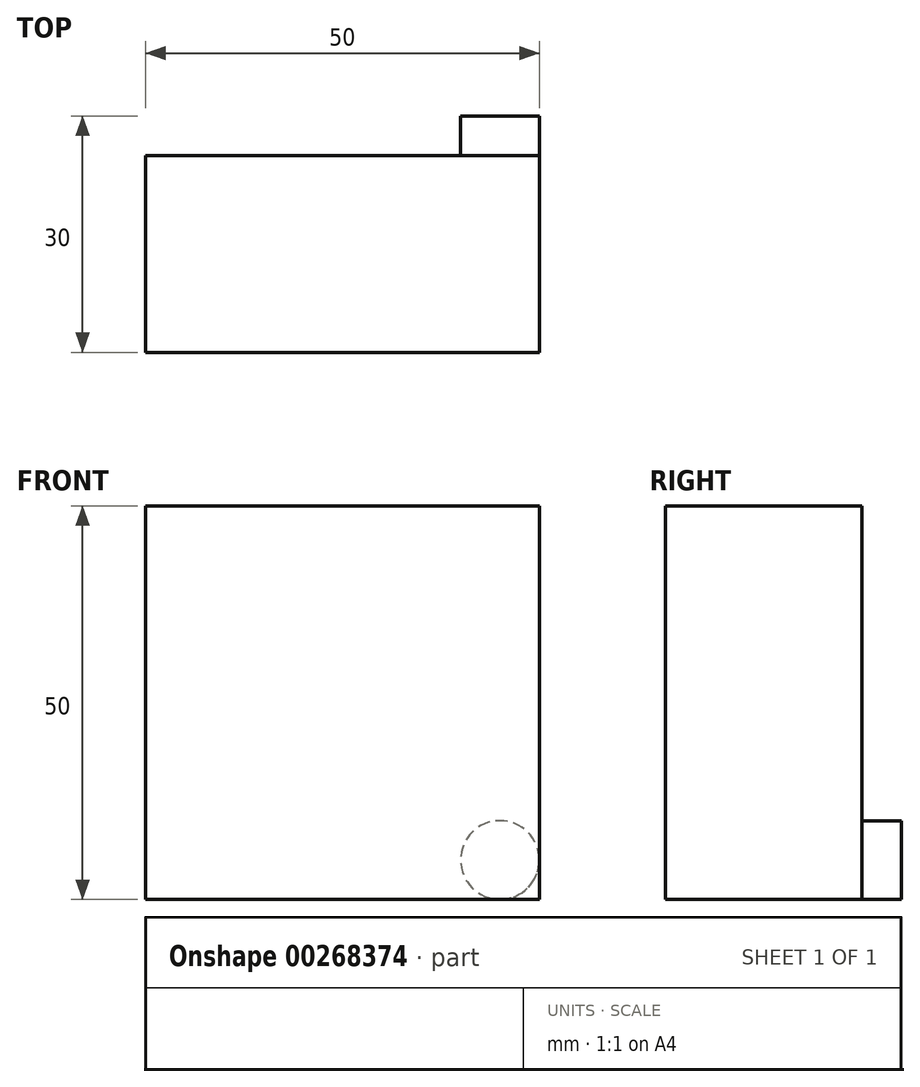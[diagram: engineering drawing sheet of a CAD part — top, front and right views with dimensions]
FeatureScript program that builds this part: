
annotation { "Feature Type Name" : "Feature", "Feature Type Description" : "" }
export const myFeature = defineFeature(function(context is Context, id is Id, definition is map)
    precondition{}
    {
        {
            var Q0;
            Q0=qCreatedBy(makeId("Front.planeOp"),FACE);
            var sketch = newSketch(context, id + "F0", { "sketchPlane" : qUnion([Q0])});
            skLineSegment(sketch, "E0.bottom", {"start": v(25, 25) * mm, "end": v(-25, 25) * mm});
            skLineSegment(sketch, "E0.top", {"start": v(25, -25) * mm, "end": v(-25, -25) * mm});
            skLineSegment(sketch, "E0.left", {"start": v(25, 25) * mm, "end": v(25, -25) * mm});
            skLineSegment(sketch, "E0.right", {"start": v(-25, 25) * mm, "end": v(-25, -25) * mm});
            skPoint(sketch, "E0.middle", {"position": v(0, 0) * mm});
            skCircle(sketch, "E1", {"center": v(20, -20) * mm, "radius": 5 * mm});
            skSolve(sketch);
        }
        {
            var Q0;
            {var subQ2=sQuery(id+"F0.wireOp",EDGE,"E0.bottom");Q0=makeQuery(id+"F0.imprint","IMPRINT",FACE,{"disambiguationData":[TD([[makeQuery(id+"F0.imprint","IMPRINT",EDGE,{"derivedFrom":subQ2}),1.0]])]});}
            var Q1;
            {var subQ0=sQuery(id+"F0.wireOp",EDGE,"E0.left");var subQ1=sQuery(id+"F0.wireOp",EDGE,"E0.top");var subQ2=makeQuery(id+"F0.imprint","INTERSECT",VERTEX,{"derivedFrom":[subQ1,subQ0]});Q1=makeQuery(id+"F0.imprint","IMPRINT",FACE,{"disambiguationData":[TD([[makeQuery(id+"F0.imprint","IMPRINT",EDGE,{"disambiguationData":[TD([[subQ2,-1.0]])],"derivedFrom":subQ1}),-1.0]])]});}
            var Q2;
            {var subQ0=sQuery(id+"F0.wireOp",EDGE,"E1");var subQ1=makeQuery(id+"F0.imprint","INTERSECT",VERTEX,{"derivedFrom":[sQuery(id+"F0.wireOp",EDGE,"E0.top"),subQ0]});Q2=makeQuery(id+"F0.imprint","IMPRINT",FACE,{"disambiguationData":[TD([[makeQuery(id+"F0.imprint","IMPRINT",EDGE,{"disambiguationData":[TD([[subQ1,1.0]])],"derivedFrom":subQ0}),1.0]])]});}
            extrude(context, id + "F1", {"entities" : qUnion([Q0, Q1, Q2]), "depth" : 25 * mm});
        }
        {
            var Q0;
            {var subQ0=sQuery(id+"F0.wireOp",EDGE,"E1");var subQ1=makeQuery(id+"F0.imprint","INTERSECT",VERTEX,{"derivedFrom":[sQuery(id+"F0.wireOp",EDGE,"E0.top"),subQ0]});Q0=makeQuery(id+"F0.imprint","IMPRINT",FACE,{"disambiguationData":[TD([[makeQuery(id+"F0.imprint","IMPRINT",EDGE,{"disambiguationData":[TD([[subQ1,1.0]])],"derivedFrom":subQ0}),1.0]])]});}
            var Q1;
            Q1=sQuery(id+"F0.wireOp",EDGE,"E1");
            extrude(context, id + "F2", {"entities" : qUnion([Q0]), "operationType" : NewBodyOperationType.ADD, "surfaceEntities" : qUnion([Q1]), "oppositeDirection" : true, "depth" : 5 * mm});
        }
    });
